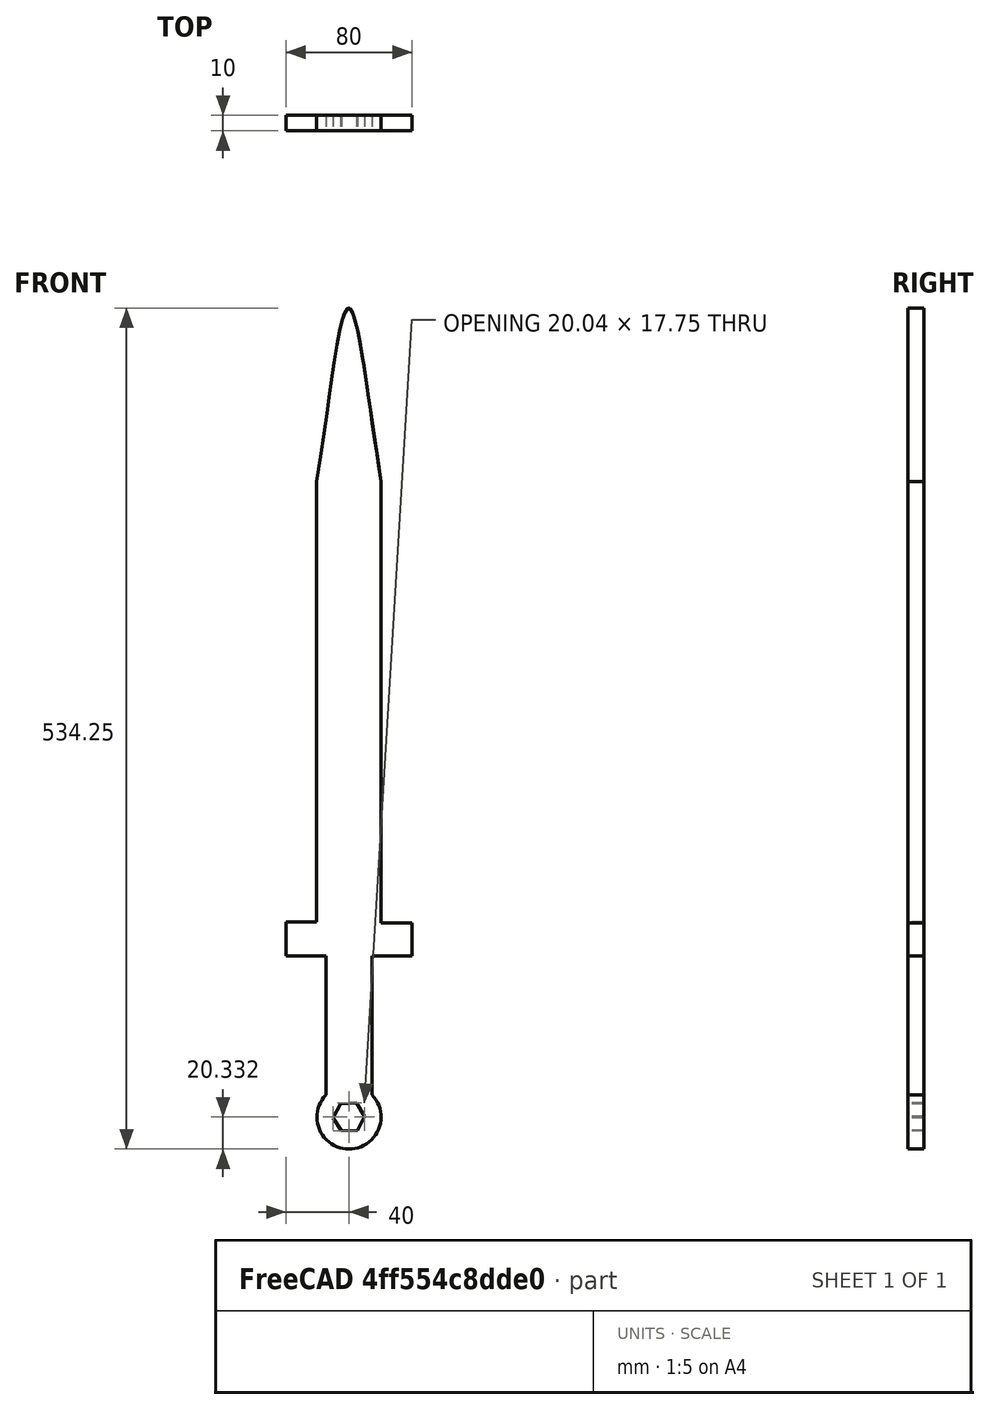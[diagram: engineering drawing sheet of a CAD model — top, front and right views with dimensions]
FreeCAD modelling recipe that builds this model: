
FCSTD DOCUMENT  (FreeCAD 0.21R33771 (Git))
Label: knife1
License: All rights reserved
LicenseURL: http://en.wikipedia.org/wiki/All_rights_reserved
objects: Sketcher::SketchObject×1, PartDesign::Pad×1, PartDesign::Body×1
note: 4 computed .brp shape members not serialized (recipe doc carries the construction recipe); baked Part::Feature solids carry a one-line shape summary decoded from their .brp

FEATURE [Sketcher::SketchObject] Sketch
  FullyConstrained = false
  MapMode = 5
  Placement = pos=(0,0,0) rot=(1,0,0;1.5708rad)
  Support = -> [XZ_Plane]
  sketch-geometry (34):
    g0: LineSegment StartX=-20.4562 StartY=-134.985 StartZ=0 EndX=-20.4562 EndY=144.526 EndZ=0
    g1: LineSegment StartX=20.4562 StartY=144.526 StartZ=0 EndX=20.4562 EndY=-135.8 EndZ=0
    g2: GeomPoint X=3.1e-13 Y=-0.205522 Z=0
    g3: GeomPoint X=-0.193928 Y=270.808 Z=0
    g4-g10: Circle x7 (B-spline internal-alignment scaffolding for g11; pole/knot coordinates omitted)
    g11: BSplineCurve PolesCount=7 KnotsCount=5 Degree=3 IsPeriodic=0
    g12-g16: GeomPoint x5 (B-spline internal-alignment scaffolding for g11; pole/knot coordinates omitted)
    g17: LineSegment StartX=-40 StartY=-134.985 StartZ=0 EndX=-40 EndY=-156.629 EndZ=0
    g18: LineSegment StartX=-40 StartY=-156.629 StartZ=0 EndX=-14.6579 EndY=-156.629 EndZ=0
    g19: LineSegment StartX=40 StartY=-156.629 StartZ=0 EndX=40 EndY=-135.8 EndZ=0
    g20: LineSegment StartX=40 StartY=-135.8 StartZ=0 EndX=20.4562 EndY=-135.8 EndZ=0
    g21: LineSegment StartX=-20.4562 StartY=-134.985 StartZ=0 EndX=-40 EndY=-134.985 EndZ=0
    g22: LineSegment StartX=-14.6579 StartY=-156.629 StartZ=0 EndX=-14.6579 EndY=-244.979 EndZ=0
    g23: LineSegment StartX=14.6579 StartY=-244.979 StartZ=0 EndX=14.6579 EndY=-156.629 EndZ=0
    g24: GeomPoint X=6.665e-13 Y=-156.629 Z=0
    g25: ArcOfCircle CenterX=0 CenterY=-259.068 CenterZ=0 NormalX=0 NormalY=0 NormalZ=1 AngleXU=0 Radius=20.3308 StartAngle=2.376 EndAngle=7.04878
    g26: LineSegment StartX=14.6579 StartY=-156.629 StartZ=0 EndX=40 EndY=-156.629 EndZ=0
    g27: LineSegment StartX=5.35259 StartY=-267.547 StartZ=0 EndX=10.0197 EndY=-258.672 EndZ=0
    g28: LineSegment StartX=10.0197 StartY=-258.672 StartZ=0 EndX=4.66711 EndY=-250.193 EndZ=0
    g29: LineSegment StartX=4.66711 StartY=-250.193 StartZ=0 EndX=-5.35259 EndY=-250.588 EndZ=0
    g30: LineSegment StartX=-5.35259 StartY=-250.588 StartZ=0 EndX=-10.0197 EndY=-259.464 EndZ=0
    g31: LineSegment StartX=-10.0197 StartY=-259.464 StartZ=0 EndX=-4.66711 EndY=-267.943 EndZ=0
    g32: LineSegment StartX=-4.66711 StartY=-267.943 StartZ=0 EndX=5.35259 EndY=-267.547 EndZ=0
    g33: Circle CenterX=0 CenterY=-259.068 CenterZ=0 NormalX=0 NormalY=0 NormalZ=1 AngleXU=0 Radius=10.0275
  constraints (47):
    c: Vertical(g0)
    c: Vertical(g1)
    c: Weight(g4) = 1
    c: Coincident(g11,g0)
    c: Equal(g4,g5)
    c: Equal(g4,g6)
    c: Equal(g4,g7)
    c: Coincident(g7,g3)
    c: Equal(g4,g8)
    c: Equal(g4,g9)
    c: Equal(g4,g10)
    c: InternalAlignment(g4-g10 -> g11) x7
    c: InternalAlignment(g12-g16 -> g11) x5
    c: Symmetric(g5,g9,g-2)
    c: Coincident(g17,g18)
    c: Coincident(g26,g19)
    c: Coincident(g19,g20)
    c: Coincident(g21,g17)
    c: Horizontal(g18)
    c: Horizontal(g20)
    c: Vertical(g17)
    c: Vertical(g19)
    c: Coincident(g0,g21)
    c: Coincident(g1,g20)
    c: Vertical(g22)
    c: Vertical(g23)
    c: PointOnObject(g24,g18)
    c: PointOnObject(g25,g-2)
    c: Coincident(g25,g22)
    c: Coincident(g23,g25)
    c: Coincident(g18,g22)
    c: Coincident(g26,g23)
    c: Coincident(g27,g28)
    c: Coincident(g28,g29)
    c: Coincident(g29,g30)
    c: Coincident(g30,g31)
    c: Coincident(g31,g32)
    c: Coincident(g32,g27)
    c: Equal(g27, g28-g32) x5
    c: PointOnObject(g27,g33)
    c: PointOnObject(g28,g33)
    c: PointOnObject(g29,g33)
    c: PointOnObject(g30,g33)
    c: PointOnObject(g31,g33)
    c: PointOnObject(g32,g33)
    c: Coincident(g33,g25)
    c: Coincident(g1,g11)
FEATURE [PartDesign::Pad] Pad
  Direction = (0,-1,2e-16)
  Length = 10
  Length2 = 10
  Placement = pos=(0,0,0) rot=(1,0,0;1.5708rad)
  Profile = -> Sketch
  ReferenceAxis = -> Sketch [N_Axis]
  Refine = true
  Type = 0
FEATURE [PartDesign::Body] Body
  Group = -> [Sketch,Pad]
  Origin = -> Origin
  Tip = -> Pad
